# Revit family: PRD_FrankeWS_UrnlDvdrs_CampusUrinalDivider_CMPX560
name_source: partatom
category: Furniture
revit_build: Autodesk Revit 2018 (Build: 20190510_1515(x64)
units: mm (PartAtom-declared; Revit-internal decimal feet)

## family parameters
Cut with Voids When Loaded = No
Host = Face
OmniClass Number = 23.40.20.21
OmniClass Title = Toilet and Bath Specialties
Room Calculation Point = No
Shared = No

## types (1)
- CMPX560
    AssetType = Fixed
    BIMObjectName = PRD_AR_UrinalDividers_CampusUrinalDivider_CMPX560
    Category = Pr_40_20_93_74, Urinal dividers
    Color = Stainless steel
    Default Elevation = 1200 mm
    Description = Urinal divider for wall mounting, stainless steel, surface satin finished, material thickness 1.5 mm, 32 mm pipe diameter, with two stainless steel covers for hidden mounting, included screws and dowels.
    DividerMaterial = PRD_AR_StainlessSteel_SatinFinished
    DurationUnit = year
    Features = stainless steel, 1.50 mm, satin finished, wall mounting, 81x760x397 mm (WxHxD)
    Finish = Satin finished
    GrossWeight = 5.85 kg
    IfcExportAs = IfcFurnitureType
    IfcExportType = NOTDEFINED
    MainColor = Stainless steel
    Manufacturer = KWC Group AG
    ManufacturerName = KWC Group AG
    ManufacturerURL = www.kwc.com
    Material = Stainless steel
    MaterialFinish = Satin finished
    MaterialThickness = 1.5 mm  [stored 0.00492126 ft]
    MaterialsBody = Stainless steel 1.4301
    Model = CMPX560
    ModelNumber = 2000056972
    ModelReference = CMPX560
    NBSDescription = Urinal divider
    NBSReference = 45-35-70/358
    Name = CAMPUS urinal divider CMPX560
    NetWeight = 4.90 kg
    NominalDepth = 397 mm  [stored 1.30249 ft]
    NominalHeight = 760 mm
    NominalLength = 81 mm  [stored 0.265748 ft]
    NominalWidth = 81 mm  [stored 0.265748 ft]
    OverallDepth = 397 mm  [stored 1.30249 ft]
    OverallHeight = 760 mm
    OverallWidth = 81 mm  [stored 0.265748 ft]
    PipeDiameter = 32 mm  [stored 0.104987 ft]
    ProductInformation = https://pim.kwc.com
    RailRadius = 70 mm  [stored 0.229659 ft]
    Size = 81x760x397 mm
    Style = Urinal divider
    TypeOfMounting = Wall mounting
    URL = www.kwc.com
    Uniclass2015Code = Pr_40_20_93_74
    Uniclass2015Title = Urinal divider
    Uniclass2015Version = Products v1.7
    Version = 1
    WarrantyDurationUnit = year

note: [stored X ft] marks values corroborated as IEEE doubles in the binary element streams (Revit-internal decimal feet)

## geometry (parser evidence)
native form markers: Sweep x2
no freeform markers — native parametric forms only
